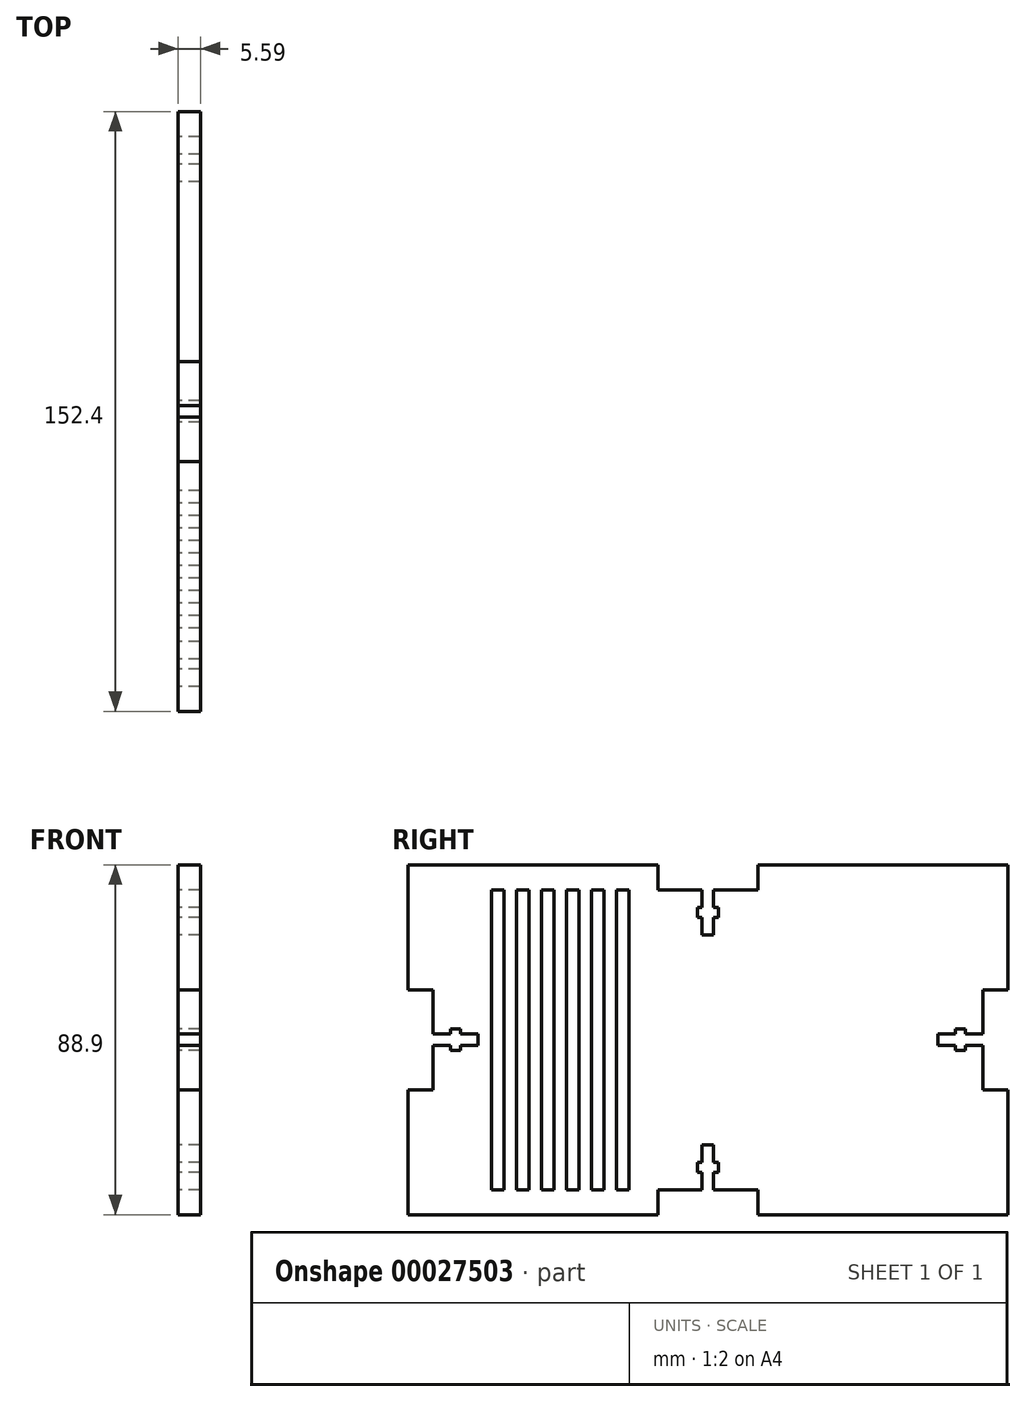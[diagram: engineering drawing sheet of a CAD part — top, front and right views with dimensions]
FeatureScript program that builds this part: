
annotation { "Feature Type Name" : "Feature", "Feature Type Description" : "" }
export const myFeature = defineFeature(function(context is Context, id is Id, definition is map)
    precondition{}
    {
        {
            var Q0;
            Q0=qCreatedBy(makeId("Right.planeOp"),FACE);
            var sketch = newSketch(context, id + "F0", { "sketchPlane" : qUnion([Q0])});
            skLineSegment(sketch, "E0.rect.bottom", {"start": v(76.2, 44.45) * mm, "end": v(12.7, 44.45) * mm});
            skLineSegment(sketch, "E0.rect.top", {"start": v(76.2, -44.45) * mm, "end": v(12.7, -44.45) * mm});
            skLineSegment(sketch, "E0.rect.left", {"start": v(76.2, 44.45) * mm, "end": v(76.2, 12.7) * mm});
            skLineSegment(sketch, "E0.rect.right", {"start": v(-76.2, 44.45) * mm, "end": v(-76.2, 12.7) * mm});
            skPoint(sketch, "E0.rect.middle", {"position": v(0, 0) * mm});
            skLineSegment(sketch, "E1", {"start": v(-76.2, 0) * mm, "end": v(0, 0) * mm, "construction": true});
            skLineSegment(sketch, "E2", {"start": v(0, 0) * mm, "end": v(76.2, 0) * mm, "construction": true});
            skLineSegment(sketch, "E3", {"start": v(38.1, 0) * mm, "end": v(38.1, -15.88) * mm, "construction": true});
            skPoint(sketch, "E4.rect.middle", {"position": v(38.1, -22.22) * mm});
            skLineSegment(sketch, "E5.0", {"start": v(29.84, 0) * mm, "end": v(29.84, -44.45) * mm, "construction": true});
            skLineSegment(sketch, "E6.0", {"start": v(46.35, 0) * mm, "end": v(46.35, -44.45) * mm, "construction": true});
            skLineSegment(sketch, "E7.0", {"start": v(50.1, -34.92) * mm, "end": v(24.7, -34.92) * mm, "construction": true});
            skLineSegment(sketch, "E8", {"start": v(38.1, 0) * mm, "end": v(38.1, 44.45) * mm, "construction": true});
            skPoint(sketch, "E9.rect.middle", {"position": v(38.1, 22.23) * mm});
            skPoint(sketch, "E10.visualSharp", {"position": v(24.77, -15.88) * mm});
            skPoint(sketch, "E11.visualSharp", {"position": v(51.44, -15.88) * mm});
            skPoint(sketch, "E12.visualSharp", {"position": v(51.44, -28.58) * mm});
            skPoint(sketch, "E13.visualSharp", {"position": v(24.77, -28.58) * mm});
            skPoint(sketch, "E14.visualSharp", {"position": v(29.85, -34.92) * mm});
            skPoint(sketch, "E15.visualSharp", {"position": v(46.36, -34.92) * mm});
            skLineSegment(sketch, "E16", {"start": v(38.1, -15.88) * mm, "end": v(38.1, -34.92) * mm, "construction": true});
            skLineSegment(sketch, "E17", {"start": v(38.1, -34.92) * mm, "end": v(38.1, -44.45) * mm, "construction": true});
            skLineSegment(sketch, "E18", {"start": v(19.69, -25.4) * mm, "end": v(56.52, -25.4) * mm, "construction": true});
            skPoint(sketch, "E18.startSnap0", {"position": v(38.1, -25.4) * mm});
            skLineSegment(sketch, "E19.0", {"start": v(-69.85, 38.1) * mm, "end": v(-69.85, -38.1) * mm, "construction": true});
            skLineSegment(sketch, "E19.1", {"start": v(69.85, 38.1) * mm, "end": v(1.46, 38.1) * mm, "construction": true});
            skLineSegment(sketch, "E19.2", {"start": v(69.85, 38.1) * mm, "end": v(69.85, -38.1) * mm, "construction": true});
            skLineSegment(sketch, "E19.3", {"start": v(69.85, -38.1) * mm, "end": v(-69.85, -38.1) * mm, "construction": true});
            skLineSegment(sketch, "E20", {"start": v(0, 44.45) * mm, "end": v(0, 38.1) * mm, "construction": true});
            skLineSegment(sketch, "E21.0", {"start": v(-12.7, 44.45) * mm, "end": v(-12.7, 38.1) * mm, "construction": true});
            skLineSegment(sketch, "E22.0", {"start": v(12.7, 44.45) * mm, "end": v(12.7, -44.45) * mm, "construction": true});
            skLineSegment(sketch, "E23.0", {"start": v(-76.2, -12.7) * mm, "end": v(0, -12.7) * mm, "construction": true});
            skLineSegment(sketch, "E24.0", {"start": v(-76.2, 12.7) * mm, "end": v(-69.85, 12.7) * mm, "construction": true});
            skLineSegment(sketch, "E25", {"start": v(-12.7, 26.67) * mm, "end": v(12.7, 26.67) * mm, "construction": true});
            skLineSegment(sketch, "E26", {"start": v(-12.7, 38.1) * mm, "end": v(-12.7, 26.67) * mm, "construction": true});
            skLineSegment(sketch, "E27", {"start": v(-12.7, 26.67) * mm, "end": v(-12.7, -44.45) * mm, "construction": true});
            skLineSegment(sketch, "E28", {"start": v(-12.7, 32.38) * mm, "end": v(12.7, 32.38) * mm, "construction": true});
            skLineSegment(sketch, "E29.0", {"start": v(-1.46, 44.45) * mm, "end": v(-1.46, -44.45) * mm, "construction": true});
            skLineSegment(sketch, "E30.0", {"start": v(1.46, 44.45) * mm, "end": v(1.46, -44.45) * mm, "construction": true});
            skLineSegment(sketch, "E31.0", {"start": v(-2.7, 44.45) * mm, "end": v(-2.7, -44.45) * mm, "construction": true});
            skLineSegment(sketch, "E32.MirrorCS", {"start": v(2.7, 44.45) * mm, "end": v(2.7, -44.45) * mm, "construction": true});
            skLineSegment(sketch, "E33.0", {"start": v(-12.7, 31.11) * mm, "end": v(12.7, 31.11) * mm, "construction": true});
            skLineSegment(sketch, "E34.MirrorCS", {"start": v(-12.7, 33.65) * mm, "end": v(12.7, 33.65) * mm, "construction": true});
            skLineSegment(sketch, "E35", {"start": v(-1.46, 44.45) * mm, "end": v(-1.46, 33.65) * mm, "construction": true});
            skLineSegment(sketch, "E36", {"start": v(-1.46, 33.65) * mm, "end": v(-2.7, 33.65) * mm, "construction": true});
            skLineSegment(sketch, "E37", {"start": v(-2.7, 33.65) * mm, "end": v(-2.7, 31.11) * mm, "construction": true});
            skLineSegment(sketch, "E38", {"start": v(-2.7, 31.11) * mm, "end": v(-1.46, 31.11) * mm, "construction": true});
            skLineSegment(sketch, "E39", {"start": v(-1.46, 31.11) * mm, "end": v(-1.46, 26.67) * mm, "construction": true});
            skLineSegment(sketch, "E40", {"start": v(-1.46, 26.67) * mm, "end": v(1.46, 26.67) * mm, "construction": true});
            skLineSegment(sketch, "E41", {"start": v(1.46, 26.67) * mm, "end": v(1.46, 31.11) * mm, "construction": true});
            skLineSegment(sketch, "E42", {"start": v(1.46, 31.11) * mm, "end": v(2.7, 31.11) * mm, "construction": true});
            skLineSegment(sketch, "E43", {"start": v(2.7, 31.11) * mm, "end": v(2.7, 33.65) * mm, "construction": true});
            skLineSegment(sketch, "E44", {"start": v(2.7, 33.65) * mm, "end": v(1.46, 33.65) * mm, "construction": true});
            skLineSegment(sketch, "E45", {"start": v(1.46, 33.65) * mm, "end": v(1.46, 44.45) * mm, "construction": true});
            skLineSegment(sketch, "E46", {"start": v(-1.46, 38.1) * mm, "end": v(-1.46, 33.65) * mm});
            skLineSegment(sketch, "E47", {"start": v(-2.7, 33.65) * mm, "end": v(-2.7, 31.11) * mm});
            skLineSegment(sketch, "E48", {"start": v(-1.46, 31.11) * mm, "end": v(-1.46, 26.67) * mm});
            skLineSegment(sketch, "E49", {"start": v(1.46, 26.67) * mm, "end": v(1.46, 31.11) * mm});
            skLineSegment(sketch, "E50", {"start": v(2.7, 31.11) * mm, "end": v(2.7, 33.65) * mm});
            skLineSegment(sketch, "E51", {"start": v(1.46, 33.65) * mm, "end": v(1.46, 38.1) * mm});
            skLineSegment(sketch, "E52", {"start": v(-1.46, 26.67) * mm, "end": v(1.46, 26.67) * mm});
            skLineSegment(sketch, "E53", {"start": v(1.46, 33.65) * mm, "end": v(2.7, 33.65) * mm});
            skLineSegment(sketch, "E54", {"start": v(1.46, 31.11) * mm, "end": v(2.7, 31.11) * mm});
            skLineSegment(sketch, "E55", {"start": v(-1.46, 31.11) * mm, "end": v(-2.7, 31.11) * mm});
            skLineSegment(sketch, "E56", {"start": v(-2.7, 33.65) * mm, "end": v(-1.46, 33.65) * mm});
            skLineSegment(sketch, "E57.MirrorCS", {"start": v(1.46, -33.65) * mm, "end": v(1.46, -38.1) * mm});
            skLineSegment(sketch, "E58.MirrorCS", {"start": v(-1.46, -38.1) * mm, "end": v(-1.46, -33.65) * mm});
            skLineSegment(sketch, "E59.MirrorCS", {"start": v(-2.7, -33.65) * mm, "end": v(-1.46, -33.65) * mm});
            skLineSegment(sketch, "E60.MirrorCS", {"start": v(-2.7, -33.65) * mm, "end": v(-2.7, -31.11) * mm});
            skLineSegment(sketch, "E61.MirrorCS", {"start": v(-1.46, -31.11) * mm, "end": v(-2.7, -31.11) * mm});
            skLineSegment(sketch, "E62.MirrorCS", {"start": v(-1.46, -31.11) * mm, "end": v(-1.46, -26.67) * mm});
            skLineSegment(sketch, "E63.MirrorCS", {"start": v(-1.46, -26.67) * mm, "end": v(1.46, -26.67) * mm});
            skLineSegment(sketch, "E64.MirrorCS", {"start": v(1.46, -26.67) * mm, "end": v(1.46, -31.11) * mm});
            skLineSegment(sketch, "E65.MirrorCS", {"start": v(1.46, -31.11) * mm, "end": v(2.7, -31.11) * mm});
            skLineSegment(sketch, "E66.MirrorCS", {"start": v(2.7, -31.11) * mm, "end": v(2.7, -33.65) * mm});
            skLineSegment(sketch, "E67.MirrorCS", {"start": v(1.46, -33.65) * mm, "end": v(2.7, -33.65) * mm});
            skLineSegment(sketch, "E68", {"start": v(-12.7, -44.45) * mm, "end": v(-12.7, -38.1) * mm});
            skLineSegment(sketch, "E69", {"start": v(-12.7, -38.1) * mm, "end": v(-1.46, -38.1) * mm});
            skLineSegment(sketch, "E70", {"start": v(12.7, -38.1) * mm, "end": v(12.7, -44.45) * mm});
            skLineSegment(sketch, "E71.trimOffspring", {"start": v(-12.7, -44.45) * mm, "end": v(-76.2, -44.45) * mm});
            skPoint(sketch, "E72.orphan", {"position": v(-1.46, -44.45) * mm});
            skPoint(sketch, "E73.orphan", {"position": v(1.46, -44.45) * mm});
            skLineSegment(sketch, "E74.trimOffspring", {"start": v(1.46, -38.1) * mm, "end": v(12.7, -38.1) * mm});
            skLineSegment(sketch, "E75", {"start": v(-12.7, 44.45) * mm, "end": v(-12.7, 38.1) * mm});
            skLineSegment(sketch, "E76", {"start": v(-12.7, 38.1) * mm, "end": v(-1.46, 38.1) * mm});
            skLineSegment(sketch, "E77", {"start": v(12.7, 38.1) * mm, "end": v(12.7, 44.45) * mm});
            skLineSegment(sketch, "E78.trimOffspring", {"start": v(-12.7, 44.45) * mm, "end": v(-76.2, 44.45) * mm});
            skLineSegment(sketch, "E79.trimOffspring", {"start": v(1.46, 38.1) * mm, "end": v(12.7, 38.1) * mm});
            skLineSegment(sketch, "E80.trimOffspring", {"start": v(0, 32.38) * mm, "end": v(0, 31.11) * mm, "construction": true});
            skLineSegment(sketch, "E81.trimOffspring", {"start": v(-1.46, 38.1) * mm, "end": v(-69.85, 38.1) * mm, "construction": true});
            skLineSegment(sketch, "E82.trimOffspring", {"start": v(0, 26.67) * mm, "end": v(0, -44.45) * mm, "construction": true});
            skLineSegment(sketch, "E83.0", {"start": v(-76.2, -1.46) * mm, "end": v(0, -1.46) * mm, "construction": true});
            skLineSegment(sketch, "E84.MirrorCS", {"start": v(-76.2, 1.46) * mm, "end": v(0, 1.46) * mm, "construction": true});
            skLineSegment(sketch, "E85.0", {"start": v(-76.2, -2.7) * mm, "end": v(0, -2.7) * mm, "construction": true});
            skLineSegment(sketch, "E86.MirrorCS", {"start": v(-76.2, 2.7) * mm, "end": v(0, 2.7) * mm, "construction": true});
            skLineSegment(sketch, "E87", {"start": v(-58.42, 12.7) * mm, "end": v(-58.42, -12.7) * mm, "construction": true});
            skLineSegment(sketch, "E88", {"start": v(-69.85, 12.7) * mm, "end": v(-58.42, 12.7) * mm, "construction": true});
            skLineSegment(sketch, "E89", {"start": v(-58.42, 12.7) * mm, "end": v(0, 12.7) * mm, "construction": true});
            skLineSegment(sketch, "E90", {"start": v(-64.13, 12.7) * mm, "end": v(-64.13, -12.7) * mm, "construction": true});
            skLineSegment(sketch, "E91.0", {"start": v(-65.4, 12.7) * mm, "end": v(-65.4, 1.46) * mm});
            skLineSegment(sketch, "E92.MirrorCS", {"start": v(-62.86, 12.7) * mm, "end": v(-62.86, -12.7) * mm, "construction": true});
            skLineSegment(sketch, "E93", {"start": v(-69.85, 1.46) * mm, "end": v(-65.4, 1.46) * mm});
            skLineSegment(sketch, "E94", {"start": v(-65.4, 1.46) * mm, "end": v(-65.4, 2.7) * mm});
            skLineSegment(sketch, "E95", {"start": v(-65.4, 2.7) * mm, "end": v(-62.86, 2.7) * mm});
            skLineSegment(sketch, "E96", {"start": v(-62.86, 2.7) * mm, "end": v(-62.86, 1.46) * mm});
            skLineSegment(sketch, "E97", {"start": v(-62.86, 1.46) * mm, "end": v(-58.42, 1.46) * mm});
            skLineSegment(sketch, "E98", {"start": v(-58.42, 1.46) * mm, "end": v(-58.42, -1.46) * mm});
            skLineSegment(sketch, "E99", {"start": v(-58.42, -1.46) * mm, "end": v(-62.86, -1.46) * mm});
            skLineSegment(sketch, "E100", {"start": v(-62.86, -1.46) * mm, "end": v(-62.86, -2.7) * mm});
            skLineSegment(sketch, "E101", {"start": v(-62.86, -2.7) * mm, "end": v(-65.4, -2.7) * mm});
            skLineSegment(sketch, "E102", {"start": v(-65.4, -2.7) * mm, "end": v(-65.4, -1.46) * mm});
            skLineSegment(sketch, "E103", {"start": v(-65.4, -1.46) * mm, "end": v(-69.85, -1.46) * mm});
            skLineSegment(sketch, "E104", {"start": v(-69.85, -1.46) * mm, "end": v(-69.85, -12.7) * mm});
            skLineSegment(sketch, "E105", {"start": v(-69.85, -12.7) * mm, "end": v(-76.2, -12.7) * mm});
            skLineSegment(sketch, "E106", {"start": v(-69.85, 1.46) * mm, "end": v(-69.85, 12.7) * mm});
            skLineSegment(sketch, "E107", {"start": v(-69.85, 12.7) * mm, "end": v(-76.2, 12.7) * mm});
            skLineSegment(sketch, "E108.trimOffspring", {"start": v(-76.2, -12.7) * mm, "end": v(-76.2, -44.45) * mm});
            skLineSegment(sketch, "E109.trimOffspring", {"start": v(-65.4, -1.46) * mm, "end": v(-65.4, -12.7) * mm});
            skLineSegment(sketch, "E110.MirrorCS", {"start": v(69.85, 12.7) * mm, "end": v(76.2, 12.7) * mm});
            skLineSegment(sketch, "E111.MirrorCS", {"start": v(69.85, 1.46) * mm, "end": v(69.85, 12.7) * mm});
            skLineSegment(sketch, "E112.MirrorCS", {"start": v(69.85, -1.46) * mm, "end": v(69.85, -12.7) * mm});
            skLineSegment(sketch, "E113.MirrorCS", {"start": v(69.85, -12.7) * mm, "end": v(76.2, -12.7) * mm});
            skLineSegment(sketch, "E114.MirrorCS", {"start": v(65.4, -1.46) * mm, "end": v(69.85, -1.46) * mm});
            skLineSegment(sketch, "E115.MirrorCS", {"start": v(65.4, -2.7) * mm, "end": v(65.4, -1.46) * mm});
            skLineSegment(sketch, "E116.MirrorCS", {"start": v(62.86, -2.7) * mm, "end": v(65.4, -2.7) * mm});
            skLineSegment(sketch, "E117.MirrorCS", {"start": v(62.86, -1.46) * mm, "end": v(62.86, -2.7) * mm});
            skLineSegment(sketch, "E118.MirrorCS", {"start": v(58.42, -1.46) * mm, "end": v(62.86, -1.46) * mm});
            skLineSegment(sketch, "E119.MirrorCS", {"start": v(58.42, 1.46) * mm, "end": v(58.42, -1.46) * mm});
            skLineSegment(sketch, "E120.MirrorCS", {"start": v(62.86, 1.46) * mm, "end": v(58.42, 1.46) * mm});
            skLineSegment(sketch, "E121.MirrorCS", {"start": v(62.86, 2.7) * mm, "end": v(62.86, 1.46) * mm});
            skLineSegment(sketch, "E122.MirrorCS", {"start": v(65.4, 2.7) * mm, "end": v(62.86, 2.7) * mm});
            skLineSegment(sketch, "E123.MirrorCS", {"start": v(65.4, 1.46) * mm, "end": v(65.4, 2.7) * mm});
            skLineSegment(sketch, "E124.MirrorCS", {"start": v(69.85, 1.46) * mm, "end": v(65.4, 1.46) * mm});
            skLineSegment(sketch, "E125.trimOffspring", {"start": v(76.2, -12.7) * mm, "end": v(76.2, -44.45) * mm});
            skLineSegment(sketch, "E126.bottom", {"start": v(-55.01, 38.1) * mm, "end": v(-51.84, 38.1) * mm});
            skLineSegment(sketch, "E126.top", {"start": v(-55.01, -38.1) * mm, "end": v(-51.84, -38.1) * mm});
            skLineSegment(sketch, "E126.left", {"start": v(-55.01, 38.1) * mm, "end": v(-55.01, -38.1) * mm});
            skLineSegment(sketch, "E126.right", {"start": v(-51.84, 38.1) * mm, "end": v(-51.84, -38.1) * mm});
            skLineSegment(sketch, "E127.0", {"start": v(-48.66, 38.1) * mm, "end": v(-48.66, -38.1) * mm, "construction": true});
            skLineSegment(sketch, "E128.bottom", {"start": v(-48.66, 38.1) * mm, "end": v(-45.49, 38.1) * mm});
            skLineSegment(sketch, "E128.top", {"start": v(-48.66, -38.1) * mm, "end": v(-45.49, -38.1) * mm});
            skLineSegment(sketch, "E128.left", {"start": v(-48.66, 38.1) * mm, "end": v(-48.66, -38.1) * mm});
            skLineSegment(sketch, "E128.right", {"start": v(-45.49, 38.1) * mm, "end": v(-45.49, -38.1) * mm});
            skLineSegment(sketch, "E129.0", {"start": v(-42.31, 38.1) * mm, "end": v(-42.31, -38.1) * mm, "construction": true});
            skLineSegment(sketch, "E130.bottom", {"start": v(-42.31, 38.1) * mm, "end": v(-39.14, 38.1) * mm});
            skLineSegment(sketch, "E130.top", {"start": v(-42.31, -38.1) * mm, "end": v(-39.14, -38.1) * mm});
            skLineSegment(sketch, "E130.left", {"start": v(-42.31, 38.1) * mm, "end": v(-42.31, -38.1) * mm});
            skLineSegment(sketch, "E130.right", {"start": v(-39.14, 38.1) * mm, "end": v(-39.14, -38.1) * mm});
            skLineSegment(sketch, "E131.0", {"start": v(-35.96, 38.1) * mm, "end": v(-35.96, -38.1) * mm, "construction": true});
            skLineSegment(sketch, "E132.bottom", {"start": v(-35.96, 38.1) * mm, "end": v(-32.79, 38.1) * mm});
            skLineSegment(sketch, "E132.top", {"start": v(-35.96, -38.1) * mm, "end": v(-32.79, -38.1) * mm});
            skLineSegment(sketch, "E132.left", {"start": v(-35.96, 38.1) * mm, "end": v(-35.96, -38.1) * mm});
            skLineSegment(sketch, "E132.right", {"start": v(-32.79, 38.1) * mm, "end": v(-32.79, -38.1) * mm});
            skLineSegment(sketch, "E133.0", {"start": v(-29.61, 38.1) * mm, "end": v(-29.61, -38.1) * mm, "construction": true});
            skLineSegment(sketch, "E134.bottom", {"start": v(-29.61, 38.1) * mm, "end": v(-26.44, 38.1) * mm});
            skLineSegment(sketch, "E134.top", {"start": v(-29.61, -38.1) * mm, "end": v(-26.44, -38.1) * mm});
            skLineSegment(sketch, "E134.left", {"start": v(-29.61, 38.1) * mm, "end": v(-29.61, -38.1) * mm});
            skLineSegment(sketch, "E134.right", {"start": v(-26.44, 38.1) * mm, "end": v(-26.44, -38.1) * mm});
            skLineSegment(sketch, "E135.0", {"start": v(-23.26, 38.1) * mm, "end": v(-23.26, -38.1) * mm, "construction": true});
            skLineSegment(sketch, "E136.bottom", {"start": v(-23.26, 38.1) * mm, "end": v(-20.09, 38.1) * mm});
            skLineSegment(sketch, "E136.top", {"start": v(-23.26, -38.1) * mm, "end": v(-20.09, -38.1) * mm});
            skLineSegment(sketch, "E136.left", {"start": v(-23.26, 38.1) * mm, "end": v(-23.26, -38.1) * mm});
            skLineSegment(sketch, "E136.right", {"start": v(-20.09, 38.1) * mm, "end": v(-20.09, -38.1) * mm});
            skSolve(sketch);
        }
        {
            var Q0;
            Q0=makeQuery(id+"F0.imprint","IMPRINT",FACE,{"disambiguationData":[TD([[makeQuery(id+"F0.imprint","IMPRINT",EDGE,{"derivedFrom":sQuery(id+"F0.wireOp",EDGE,"E0.rect.bottom")}),1.0]])]});
            extrude(context, id + "F1", {"entities" : qUnion([Q0]), "depth" : 5.6 * mm});
        }
    });
